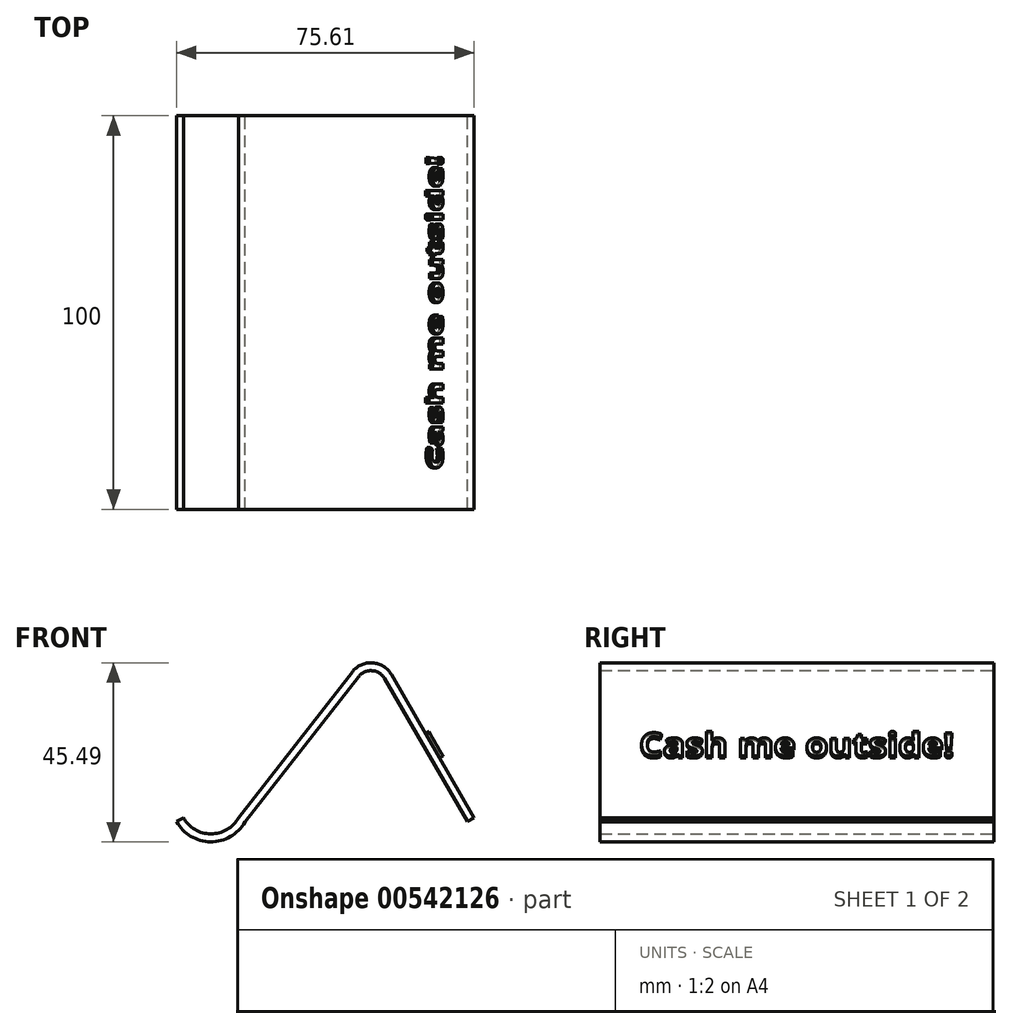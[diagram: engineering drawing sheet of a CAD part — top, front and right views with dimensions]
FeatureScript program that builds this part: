
annotation { "Feature Type Name" : "Feature", "Feature Type Description" : "" }
export const myFeature = defineFeature(function(context is Context, id is Id, definition is map)
    precondition{}
    {
        {
            var Q0;
            Q0=qCreatedBy(makeId("Front.planeOp"),FACE);
            var sketch = newSketch(context, id + "F0", { "sketchPlane" : qUnion([Q0])});
            skLineSegment(sketch, "E0", {"start": v(-5.47, 37.05) * mm, "end": v(-34.4, 0) * mm});
            skLineSegment(sketch, "E1", {"start": v(4.45, 36.36) * mm, "end": v(25.47, 0) * mm});
            skPoint(sketch, "E2.visualSharp", {"position": v(0, 44.06) * mm});
            skArc(sketch, "E2.filletArc", {"start": v(4.45, 36.36) * mm, "mid": v(-0.33, 39.35) * mm, "end": v(-5.47, 37.05) * mm});
            skArc(sketch, "E3", {"start": v(-48.4, 0) * mm, "mid": v(-41.4, -4.13) * mm, "end": v(-34.4, 0) * mm});
            skLineSegment(sketch, "E4.0", {"start": v(2.72, 35.36) * mm, "end": v(23.74, -1) * mm});
            skArc(sketch, "E4.1", {"start": v(2.72, 35.36) * mm, "mid": v(-0.47, 37.35) * mm, "end": v(-3.9, 35.82) * mm});
            skLineSegment(sketch, "E4.2", {"start": v(-3.9, 35.82) * mm, "end": v(-32.72, -1.11) * mm});
            skArc(sketch, "E4.3", {"start": v(-50.14, -0.97) * mm, "mid": v(-41.47, -6.13) * mm, "end": v(-32.72, -1.11) * mm});
            skLineSegment(sketch, "E5", {"start": v(-48.4, 0) * mm, "end": v(-50.14, -0.97) * mm});
            skLineSegment(sketch, "E6", {"start": v(23.74, -1) * mm, "end": v(25.47, 0) * mm});
            skSolve(sketch);
        }
        {
            var Q0;
            Q0=makeQuery(id+"F0.imprint","IMPRINT",FACE,{"disambiguationData":[TD([[makeQuery(id+"F0.imprint","IMPRINT",EDGE,{"derivedFrom":sQuery(id+"F0.wireOp",EDGE,"E0")}),1.0]])]});
            extrude(context, id + "F1", {"entities" : qUnion([Q0]), "depth" : 100 * mm, "offsetDistance" : 25 * mm});
        }
        {
            var Q0;
            Q0=makeQuery(id+"F1.opExtrude","SWEPT_FACE",FACE,{"disambiguationData":[OSD([sQuery(id+"F0.wireOp",EDGE,"E1")])]});
            var sketch = newSketch(context, id + "F2", { "sketchPlane" : qUnion([Q0])});
            skText(sketch, "E7", { "text": "Cash me outside!", "fontName": "OpenSans-Bold.ttf"});
            skPoint(sketch, "E8", {"position": v(-100, 8.25) * mm});
            skPoint(sketch, "E9", {"position": v(-50, -12.75) * mm});
            skPoint(sketch, "E10", {"position": v(-50, 4.87) * mm});
            skPoint(sketch, "E11", {"position": v(-90, 8.25) * mm});
            const initialGuessF2  = {"E7": [-0.09, 0.00487, 1, 0, 0.00676]};
            skSetInitialGuess(sketch, initialGuessF2);
            skSolve(sketch);
        }
        {
            var Q0;
            Q0 = qSketchRegion(id + "F2", true);
            extrude(context, id + "F3", {"entities" : qUnion([Q0]), "operationType" : NewBodyOperationType.ADD, "depth" : 1 * mm, "offsetDistance" : 25 * mm});
        }
    });
